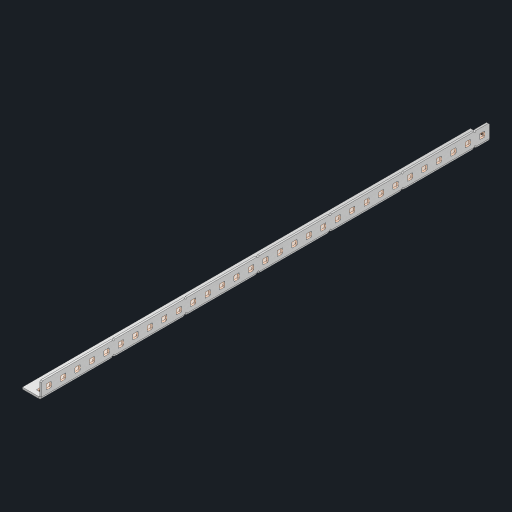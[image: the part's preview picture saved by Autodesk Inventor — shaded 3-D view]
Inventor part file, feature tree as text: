
AUTODESK INVENTOR PART (.ipt)
format: ipt  version: 2023 (Build 270158000, 158)  size: 986,624 bytes
history: native  units: in
note: dims shown in document units (in); Inventor stores cm internally (conversion verified against a paired STEP export)
features: other x67, extrude x61, sheet_metal_op x10, sketch x8, mirror x1, pattern_linear x1, chamfer x1
ambient origin geometry x8: Origin, YZ Plane, XZ Plane, XY Plane, X Axis, Y Axis, Z Axis, Center Point
bodies: Solid1 (feature_tree), Body (feature_tree)
feature tree (149):
  other  "Flange Pattern Plane"
  sheet_metal_op  "Flange Pattern"
  sheet_metal_op  "Body Pattern"
  other  "Arc Length"
  mirror  "Notch Mirror"
  pattern_linear  "Notch Pattern"  Spacing1=0.25in  [1 undecoded]
  chamfer  "End Chamfer"
  extrude  "Half Cut"  Depth=0.0625in
  sketch  "Sketch1"  dims[d0=1.5in]
  other  "Plate1"
  sketch  "Sketch2"  dims[d1=15.5in]
  other  "Plate2"
  sheet_metal_op  "Bend1"
  sheet_metal_op  "Corner1"
  sketch  "Sketch3"  dims[d2=0.0625in]
  other  "Flange Pattern Sketch"
  sketch  "Sketch7"  dims[d3=0.0625in]
  other  "Srf1"
  other  "Srf2"
  sketch  "Sketch8"  dims[d4=0.0312in]
  sketch  "Sketch9"  dims[d5=0.125in]
  other  "Srf91"
  sheet_metal_op  "Body Pattern Sketch"
  other  "Srf92"
  sketch  "Sketch13"  dims[d6=0.0625in]
  sketch  "Sketch14"  dims[d7=0.5in d8=90.0deg d9=0.0312in d10=0.25in d11=0.0625in d12=0.0625in d16=0.182in d17=0.02in d18=0.0625in d19=0.0in d20=0.25in d21=0.25in d46=0.172in d47=1.0in d48=0.0in d49=0.182in d50=0.02in d51=0.25in d52=0.25in d53=0.0625in d54=0.0in d55=0.172in d56=1.0in d57=0.0in d60=12.2047in d62=0.5in d63=0.3937in d65=0.5in d85=0.1473in d86=0.1782in d88=0.04in d89=0.0625in d90=0.0in d91=0.04in d92=0.0491in d95=2.5in d96=0.04in d97=0.25in d98=45.0deg d101=0.0in d102=2.497in d131=0.5in d132=12.2047in d134=0.5in d139=0.5in]
  other  "Srf856"
  other  "Srf1310"
  other  "Srf1311"
  other  "Srf1312"
  other  "Srf1376"
  other  "Srf1377"
  other  "Srf1728"
  other  "Srf1755"
  other  "Srf1878"
  other  "Srf1879"
  other  "Srf1880"
  other  "Srf1881"
  other  "Srf1882"
  other  "Srf1883"
  other  "Srf1884"
  other  "Srf1885"
  other  "Srf1886"
  other  "Srf1887"
  other  "Srf1888"
  other  "Srf1889"
  other  "Srf1890"
  other  "Srf1891"
  other  "Srf1892"
  other  "Srf1893"
  other  "Srf1894"
  other  "Srf1895"
  other  "Srf1896"
  other  "Srf1897"
  other  "Srf1898"
  other  "Srf1899"
  other  "Srf1900"
  other  "Srf1901"
  other  "Srf1902"
  other  "Srf1942"
  other  "Srf1943"
  other  "Srf1944"
  other  "Srf1945"
  other  "Srf1946"
  other  "Srf1947"
  other  "Srf1948"
  other  "Srf1949"
  other  "Srf1950"
  other  "Srf1951"
  other  "Srf1952"
  other  "Srf1953"
  other  "Srf1954"
  other  "Srf1955"
  other  "Srf1956"
  other  "Srf1957"
  other  "Srf1958"
  other  "Srf1959"
  other  "Srf1960"
  other  "Srf1961"
  other  "Srf1962"
  other  "Srf1963"
  other  "Srf1964"
  other  "Srf1965"
  other  "Srf1966"
  sheet_metal_op  "Flange Stamp"
  sheet_metal_op  "Flange Circle"
  sheet_metal_op  "Body Stamp"
  sheet_metal_op  "Body Circle"
  sheet_metal_op  "Notch"
  extrude  "ExtrusionSrf2"  Depth=0.0625in
  extrude  "ExtrusionSrf92"  Depth=0.5in
  extrude  "ExtrusionSrf856"  Depth=0.02in
  extrude  "ExtrusionSrf1310"  Depth=0.0625in
  extrude  "ExtrusionSrf1311"  TaperAngle=0.0deg  [1 undecoded]
  extrude  "ExtrusionSrf1312"  Depth=0.5in
  extrude  "ExtrusionSrf1376"  Depth=0.5in
  extrude  "ExtrusionSrf1377"  Depth=0.5in
  extrude  "ExtrusionSrf1728"  Depth=0.5in TaperAngle=0.0deg
  extrude  "ExtrusionSrf1755"  Depth=0.5in
  extrude  "ExtrusionSrf1878"  Depth=0.02in
  extrude  "ExtrusionSrf1879"  Depth=0.5in
  extrude  "ExtrusionSrf1880"  Depth=0.5in
  extrude  "ExtrusionSrf1881"  Depth=0.0625in
  extrude  "ExtrusionSrf1882"  TaperAngle=0.0deg  [1 undecoded]
  extrude  "ExtrusionSrf1883"  Depth=0.5in
  extrude  "ExtrusionSrf1884"  Depth=0.5in TaperAngle=0.0deg
  extrude  "ExtrusionSrf1885"  Depth=0.5in
  extrude  "ExtrusionSrf1886"  Depth=0.5in
  extrude  "ExtrusionSrf1887"  Depth=0.5in
  extrude  "ExtrusionSrf1888"  Depth=0.5in
  extrude  "ExtrusionSrf1889"  Depth=0.5in
  extrude  "ExtrusionSrf1890"  Depth=0.0625in
  extrude  "ExtrusionSrf1891"  TaperAngle=0.0deg  [1 undecoded]
  extrude  "ExtrusionSrf1892"  Depth=0.5in
  extrude  "ExtrusionSrf1893"  Depth=0.5in
  extrude  "ExtrusionSrf1894"  Depth=0.5in
  extrude  "ExtrusionSrf1895"  Depth=0.5in TaperAngle=45.0deg
  extrude  "ExtrusionSrf1896"  TaperAngle=0.0deg  [1 undecoded]
  extrude  "ExtrusionSrf1897"  Depth=0.5in
  extrude  "ExtrusionSrf1898"  Depth=0.5in
  extrude  "ExtrusionSrf1899"  Depth=0.5in
  extrude  "ExtrusionSrf1900"  Depth=0.5in
  extrude  "ExtrusionSrf1901"  Depth=0.5in
  extrude  "ExtrusionSrf1902"  [1 undecoded]
  extrude  "ExtrusionSrf1942"  [1 undecoded]
  extrude  "ExtrusionSrf1943"  [1 undecoded]
  extrude  "ExtrusionSrf1944"  [1 undecoded]
  extrude  "ExtrusionSrf1945"  [1 undecoded]
  extrude  "ExtrusionSrf1946"  [1 undecoded]
  extrude  "ExtrusionSrf1947"  [1 undecoded]
  extrude  "ExtrusionSrf1948"  [1 undecoded]
  extrude  "ExtrusionSrf1949"  [1 undecoded]
  extrude  "ExtrusionSrf1950"  [1 undecoded]
  extrude  "ExtrusionSrf1951"  [1 undecoded]
  extrude  "ExtrusionSrf1952"  [1 undecoded]
  extrude  "ExtrusionSrf1953"  [1 undecoded]
  extrude  "ExtrusionSrf1954"  [1 undecoded]
  extrude  "ExtrusionSrf1955"  [1 undecoded]
  extrude  "ExtrusionSrf1956"  [1 undecoded]
  extrude  "ExtrusionSrf1957"  [1 undecoded]
  extrude  "ExtrusionSrf1958"  [1 undecoded]
  extrude  "ExtrusionSrf1959"  [1 undecoded]
  extrude  "ExtrusionSrf1960"  [1 undecoded]
  extrude  "ExtrusionSrf1961"  [1 undecoded]
  extrude  "ExtrusionSrf1962"  [1 undecoded]
  extrude  "ExtrusionSrf1963"  [1 undecoded]
  extrude  "ExtrusionSrf1964"  [1 undecoded]
  extrude  "ExtrusionSrf1965"  [1 undecoded]
  extrude  "ExtrusionSrf1966"  [1 undecoded]
note: 31 required parameter values undecoded (feature->parameter linkage not recoverable at this tier; creation-order binding heuristic only, values carry confidence <= 0.55)
